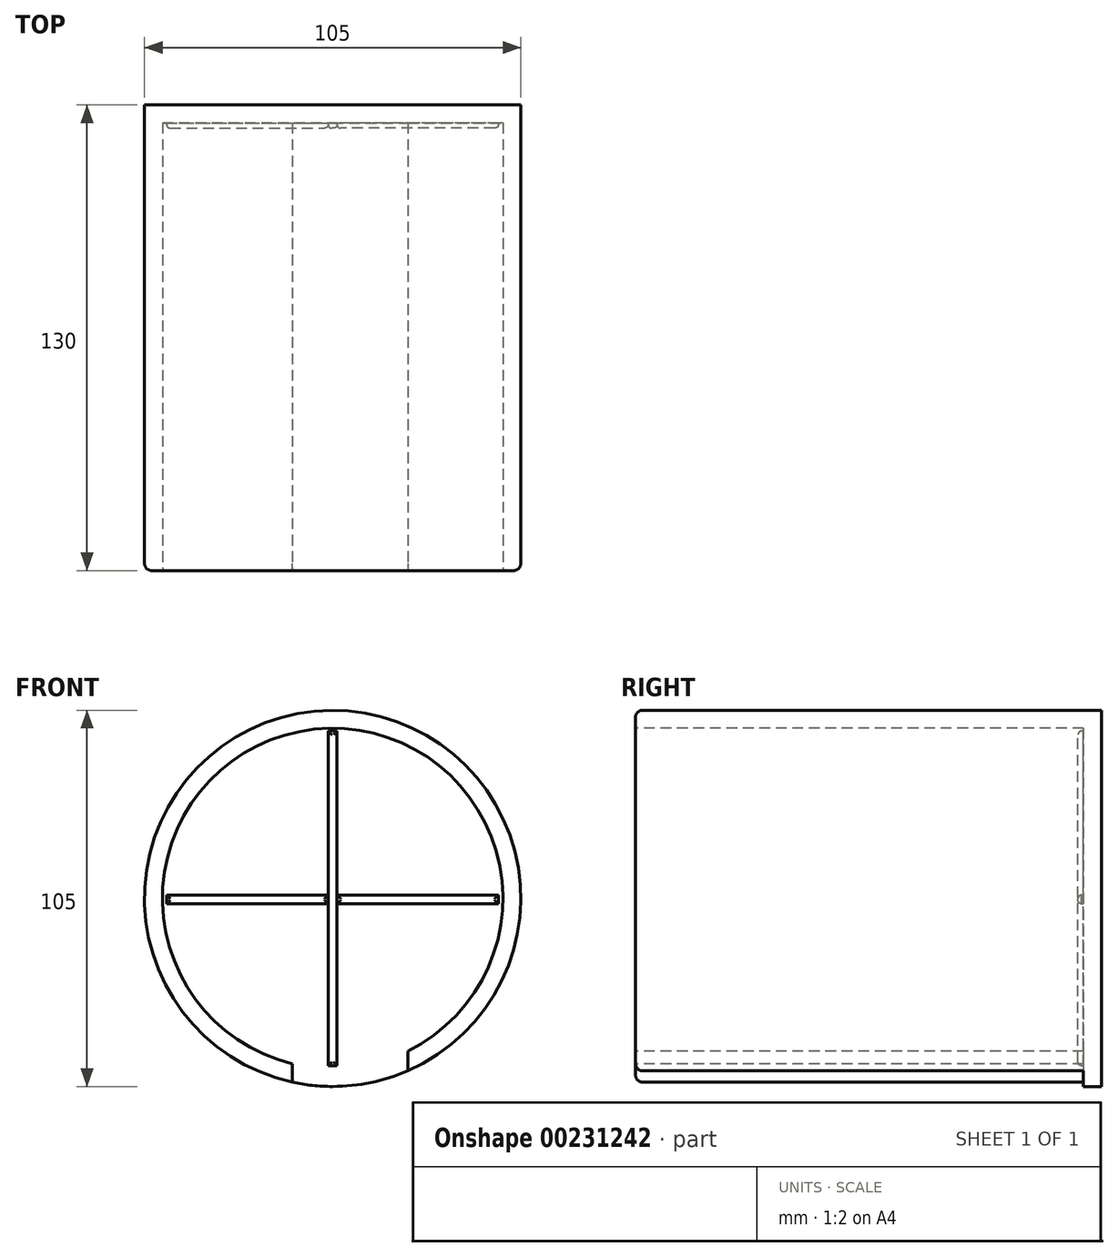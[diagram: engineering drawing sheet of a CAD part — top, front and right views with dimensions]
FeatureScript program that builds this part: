
annotation { "Feature Type Name" : "Feature", "Feature Type Description" : "" }
export const myFeature = defineFeature(function(context is Context, id is Id, definition is map)
    precondition{}
    {
        {
            var Q0;
            Q0=qCreatedBy(makeId("Front.planeOp"),FACE);
            var sketch = newSketch(context, id + "F0", { "sketchPlane" : qUnion([Q0])});
            skCircle(sketch, "E0", {"center": v(0, 0) * mm, "radius": 52.5 * mm});
            skSolve(sketch);
        }
        {
            var Q0;
            Q0=makeQuery(id+"F0.imprint","IMPRINT",FACE,{"disambiguationData":[TD([[makeQuery(id+"F0.imprint","IMPRINT",EDGE,{"derivedFrom":sQuery(id+"F0.wireOp",EDGE,"E0")}),1.0]])]});
            extrude(context, id + "F1", {"entities" : qUnion([Q0]), "oppositeDirection" : true, "depth" : 130 * mm});
        }
        {
            var Q0;
            Q0=makeQuery(id+"F1.opExtrude","CAP_FACE",FACE,{"disambiguationData":[OSD([sQuery(id+"F0.wireOp",EDGE,"E0")])],"isStart":true});
            var sketch = newSketch(context, id + "F2", { "sketchPlane" : qUnion([Q0])});
            skCircle(sketch, "E1", {"center": v(0, 0) * mm, "radius": 47.5 * mm});
            skSolve(sketch);
        }
        {
            var Q0;
            Q0=makeQuery(id+"F2.imprint","IMPRINT",FACE,{"disambiguationData":[TD([[makeQuery(id+"F2.imprint","IMPRINT",EDGE,{"derivedFrom":sQuery(id+"F2.wireOp",EDGE,"E1")}),1.0]])]});
            extrude(context, id + "F3", {"entities" : qUnion([Q0]), "operationType" : NewBodyOperationType.REMOVE, "oppositeDirection" : true, "depth" : 125 * mm});
        }
        {
            var Q0;
            Q0=makeQuery(id+"F1.opExtrude","CAP_FACE",FACE,{"disambiguationData":[OSD([sQuery(id+"F0.wireOp",EDGE,"E0")])],"isStart":true});
            var sketch = newSketch(context, id + "F4", { "sketchPlane" : qUnion([Q0])});
            skLineSegment(sketch, "E2.bottom", {"start": v(-11.25, -38.08) * mm, "end": v(20.95, -38.08) * mm});
            skLineSegment(sketch, "E2.top", {"start": v(-11.25, -55.59) * mm, "end": v(20.95, -55.59) * mm});
            skLineSegment(sketch, "E2.left", {"start": v(-11.25, -38.08) * mm, "end": v(-11.25, -55.59) * mm});
            skLineSegment(sketch, "E2.right", {"start": v(20.95, -38.08) * mm, "end": v(20.95, -55.59) * mm});
            skLineSegment(sketch, "E3.bottom", {"start": v(12.08, -38.08) * mm, "end": v(11.58, -38.08) * mm});
            skLineSegment(sketch, "E3.top", {"start": v(12.08, -37.59) * mm, "end": v(11.58, -37.59) * mm});
            skSolve(sketch);
        }
        {
            var Q0;
            {var subQ0=sQuery(id+"F4.wireOp",EDGE,"E2.left");var subQ1=makeQuery(id+"F1.opExtrude","CAP_EDGE",EDGE,{"disambiguationData":[OSD([sQuery(id+"F0.wireOp",EDGE,"E0")])],"isStart":true});var subQ2=makeQuery(id+"F4.imprint","INTERSECT",VERTEX,{"derivedFrom":[subQ1,subQ0]});Q0=makeQuery(id+"F4.imprint","IMPRINT",FACE,{"disambiguationData":[TD([[makeQuery(id+"F4.imprint","IMPRINT",EDGE,{"disambiguationData":[TD([[subQ2,1.0]])],"derivedFrom":subQ0}),1.0]])]});}
            extrude(context, id + "F5", {"entities" : qUnion([Q0]), "operationType" : NewBodyOperationType.REMOVE, "oppositeDirection" : true, "depth" : 125 * mm});
        }
        {
            var Q0;
            Q0=makeQuery(id+"F1.opExtrude","CAP_EDGE",EDGE,{"disambiguationData":[OSD([sQuery(id+"F0.wireOp",EDGE,"E0")])],"isStart":true});
            var Q1;
            Q1=makeQuery(id+"F3.boolean.opBoolean","COPY",EDGE,{"derivedFrom":makeQuery(id+"F3.opExtrude","CAP_EDGE",EDGE,{"disambiguationData":[OSD([sQuery(id+"F2.wireOp",EDGE,"E1")])],"isStart":true})});
            var Q2;
            Q2=makeQuery(id+"F5.boolean.opBoolean","COPY",EDGE,{"derivedFrom":makeQuery(id+"F5.opExtrude","SWEPT_EDGE",EDGE,{"disambiguationData":[OSD([sQuery(id+"F2.wireOp",EDGE,"E1"),sQuery(id+"F4.wireOp",EDGE,"E2.left")])]})});
            var Q3;
            Q3=makeQuery(id+"F5.boolean.opBoolean","COPY",EDGE,{"derivedFrom":makeQuery(id+"F5.opExtrude","SWEPT_EDGE",EDGE,{"disambiguationData":[OSD([sQuery(id+"F2.wireOp",EDGE,"E1"),sQuery(id+"F4.wireOp",EDGE,"E2.right")])]})});
            var Q4;
            Q4=makeQuery(id+"F5.boolean.opBoolean","COPY",EDGE,{"derivedFrom":makeQuery(id+"F5.opExtrude","SWEPT_EDGE",EDGE,{"disambiguationData":[OSD([sQuery(id+"F0.wireOp",EDGE,"E0"),sQuery(id+"F4.wireOp",EDGE,"E2.left")])]})});
            var Q5;
            Q5=makeQuery(id+"F5.boolean.opBoolean","COPY",EDGE,{"derivedFrom":makeQuery(id+"F5.opExtrude","SWEPT_EDGE",EDGE,{"disambiguationData":[OSD([sQuery(id+"F0.wireOp",EDGE,"E0"),sQuery(id+"F4.wireOp",EDGE,"E2.right")])]})});
            fillet(context, id + "F6", {"entities" : qUnion([Q0, Q1, Q2, Q3, Q4, Q5]), "radius" : 2 * mm, "tangentPropagation" : true, "allowEdgeOverflow" : false});
        }
        {
            var Q0;
            {var subQ0=sQuery(id+"F2.wireOp",EDGE,"E1");Q0=makeQuery(id+"F5.boolean.opBoolean","MERGE",FACE,{"derivedFrom":[makeQuery(id+"F3.boolean.opBoolean","COPY",FACE,{"derivedFrom":makeQuery(id+"F3.opExtrude","CAP_FACE",FACE,{"disambiguationData":[OSD([subQ0])],"isStart":false})}),makeQuery(id+"F5.opExtrude","CAP_FACE",FACE,{"disambiguationData":[OSD([sQuery(id+"F0.wireOp",EDGE,"E0"),subQ0,sQuery(id+"F4.wireOp",EDGE,"E2.left"),sQuery(id+"F4.wireOp",EDGE,"E2.right")])],"isStart":false})]});}
            var sketch = newSketch(context, id + "F7", { "sketchPlane" : qUnion([Q0])});
            skLineSegment(sketch, "E4.bottom", {"start": v(1.25, -46.72) * mm, "end": v(-1.25, -46.72) * mm});
            skLineSegment(sketch, "E4.top", {"start": v(1.25, 46.72) * mm, "end": v(-1.25, 46.72) * mm});
            skLineSegment(sketch, "E4.left", {"start": v(1.25, -46.72) * mm, "end": v(1.25, 46.72) * mm});
            skLineSegment(sketch, "E4.right", {"start": v(-1.25, -46.72) * mm, "end": v(-1.25, 46.72) * mm});
            skSolve(sketch);
        }
        {
            var Q0;
            Q0=makeQuery(id+"F7.imprint","IMPRINT",FACE,{"disambiguationData":[TD([[makeQuery(id+"F7.imprint","IMPRINT",EDGE,{"derivedFrom":sQuery(id+"F7.wireOp",EDGE,"E4.bottom")}),-1.0]])]});
            extrude(context, id + "F8", {"entities" : qUnion([Q0]), "operationType" : NewBodyOperationType.ADD, "depth" : 1.5 * mm});
        }
        {
            var Q0;
            Q0=makeQuery(id+"F8.opExtrude","CAP_EDGE",EDGE,{"disambiguationData":[OSD([sQuery(id+"F7.wireOp",EDGE,"E4.right")])],"isStart":false});
            var Q1;
            Q1=makeQuery(id+"F8.opExtrude","CAP_EDGE",EDGE,{"disambiguationData":[OSD([sQuery(id+"F7.wireOp",EDGE,"E4.left")])],"isStart":false});
            var Q2;
            Q2=makeQuery(id+"F8.opExtrude","CAP_EDGE",EDGE,{"disambiguationData":[OSD([sQuery(id+"F7.wireOp",EDGE,"E4.top")])],"isStart":false});
            var Q3;
            Q3=makeQuery(id+"F8.opExtrude","CAP_EDGE",EDGE,{"disambiguationData":[OSD([sQuery(id+"F7.wireOp",EDGE,"E4.bottom")])],"isStart":false});
            fillet(context, id + "F9", {"entities" : qUnion([Q0, Q1, Q2, Q3]), "radius" : 1 * mm, "tangentPropagation" : true, "allowEdgeOverflow" : false});
        }
        {
            var Q0;
            {var subQ0=sQuery(id+"F2.wireOp",EDGE,"E1");Q0=makeQuery(id+"F5.boolean.opBoolean","MERGE",FACE,{"derivedFrom":[makeQuery(id+"F3.boolean.opBoolean","COPY",FACE,{"derivedFrom":makeQuery(id+"F3.opExtrude","CAP_FACE",FACE,{"disambiguationData":[OSD([subQ0])],"isStart":false})}),makeQuery(id+"F5.opExtrude","CAP_FACE",FACE,{"disambiguationData":[OSD([sQuery(id+"F0.wireOp",EDGE,"E0"),subQ0,sQuery(id+"F4.wireOp",EDGE,"E2.left"),sQuery(id+"F4.wireOp",EDGE,"E2.right")])],"isStart":false})]});}
            var sketch = newSketch(context, id + "F10", { "sketchPlane" : qUnion([Q0])});
            skLineSegment(sketch, "E5.bottom", {"start": v(-46.33, 0.95) * mm, "end": v(-1.25, 0.95) * mm});
            skLineSegment(sketch, "E5.top", {"start": v(-46.33, -1.49) * mm, "end": v(-1.25, -1.49) * mm});
            skLineSegment(sketch, "E5.left", {"start": v(-46.33, 0.95) * mm, "end": v(-46.33, -1.49) * mm});
            skLineSegment(sketch, "E5.right", {"start": v(-1.25, 0.95) * mm, "end": v(-1.25, -1.49) * mm});
            skSolve(sketch);
        }
        {
            var Q0;
            Q0=makeQuery(id+"F10.imprint","IMPRINT",FACE,{"disambiguationData":[TD([[makeQuery(id+"F10.imprint","IMPRINT",EDGE,{"derivedFrom":sQuery(id+"F10.wireOp",EDGE,"E5.bottom")}),-1.0]])]});
            extrude(context, id + "F11", {"entities" : qUnion([Q0]), "operationType" : NewBodyOperationType.ADD, "depth" : 1.5 * mm});
        }
        {
            var Q0;
            Q0=makeQuery(id+"F11.opExtrude","CAP_EDGE",EDGE,{"disambiguationData":[OSD([sQuery(id+"F10.wireOp",EDGE,"E5.top")])],"isStart":false});
            var Q1;
            Q1=makeQuery(id+"F11.opExtrude","CAP_EDGE",EDGE,{"disambiguationData":[OSD([sQuery(id+"F10.wireOp",EDGE,"E5.bottom")])],"isStart":false});
            var Q2;
            Q2=makeQuery(id+"F11.opExtrude","CAP_EDGE",EDGE,{"disambiguationData":[OSD([sQuery(id+"F10.wireOp",EDGE,"E5.left")])],"isStart":false});
            var Q3;
            Q3=makeQuery(id+"F11.opExtrude","CAP_EDGE",EDGE,{"disambiguationData":[OSD([sQuery(id+"F10.wireOp",EDGE,"E5.right")])],"isStart":false});
            fillet(context, id + "F12", {"entities" : qUnion([Q0, Q1, Q2, Q3]), "radius" : 1 * mm, "tangentPropagation" : true, "allowEdgeOverflow" : false});
        }
        {
            var Q0;
            {var subQ0=sQuery(id+"F2.wireOp",EDGE,"E1");Q0=makeQuery(id+"F5.boolean.opBoolean","MERGE",FACE,{"derivedFrom":[makeQuery(id+"F3.boolean.opBoolean","COPY",FACE,{"derivedFrom":makeQuery(id+"F3.opExtrude","CAP_FACE",FACE,{"disambiguationData":[OSD([subQ0])],"isStart":false})}),makeQuery(id+"F5.opExtrude","CAP_FACE",FACE,{"disambiguationData":[OSD([sQuery(id+"F0.wireOp",EDGE,"E0"),subQ0,sQuery(id+"F4.wireOp",EDGE,"E2.left"),sQuery(id+"F4.wireOp",EDGE,"E2.right")])],"isStart":false})]});}
            var sketch = newSketch(context, id + "F13", { "sketchPlane" : qUnion([Q0])});
            skLineSegment(sketch, "E6.bottom", {"start": v(46.24, 0.9) * mm, "end": v(1.25, 0.9) * mm});
            skLineSegment(sketch, "E6.top", {"start": v(46.24, -1.53) * mm, "end": v(1.25, -1.53) * mm});
            skLineSegment(sketch, "E6.left", {"start": v(46.24, 0.9) * mm, "end": v(46.24, -1.53) * mm});
            skLineSegment(sketch, "E6.right", {"start": v(1.25, 0.9) * mm, "end": v(1.25, -1.53) * mm});
            skSolve(sketch);
        }
        {
            var Q0;
            Q0=makeQuery(id+"F13.imprint","IMPRINT",FACE,{"disambiguationData":[TD([[makeQuery(id+"F13.imprint","IMPRINT",EDGE,{"derivedFrom":sQuery(id+"F13.wireOp",EDGE,"E6.bottom")}),1.0]])]});
            extrude(context, id + "F14", {"entities" : qUnion([Q0]), "operationType" : NewBodyOperationType.ADD, "depth" : 1.5 * mm});
        }
        {
            var Q0;
            Q0=makeQuery(id+"F14.opExtrude","CAP_EDGE",EDGE,{"disambiguationData":[OSD([sQuery(id+"F13.wireOp",EDGE,"E6.bottom")])],"isStart":false});
            var Q1;
            Q1=makeQuery(id+"F14.opExtrude","CAP_EDGE",EDGE,{"disambiguationData":[OSD([sQuery(id+"F13.wireOp",EDGE,"E6.top")])],"isStart":false});
            var Q2;
            Q2=makeQuery(id+"F14.opExtrude","CAP_EDGE",EDGE,{"disambiguationData":[OSD([sQuery(id+"F13.wireOp",EDGE,"E6.right")])],"isStart":false});
            var Q3;
            Q3=makeQuery(id+"F14.opExtrude","CAP_EDGE",EDGE,{"disambiguationData":[OSD([sQuery(id+"F13.wireOp",EDGE,"E6.left")])],"isStart":false});
            fillet(context, id + "F15", {"entities" : qUnion([Q0, Q1, Q2, Q3]), "radius" : 1 * mm, "tangentPropagation" : true, "allowEdgeOverflow" : false});
        }
    });
